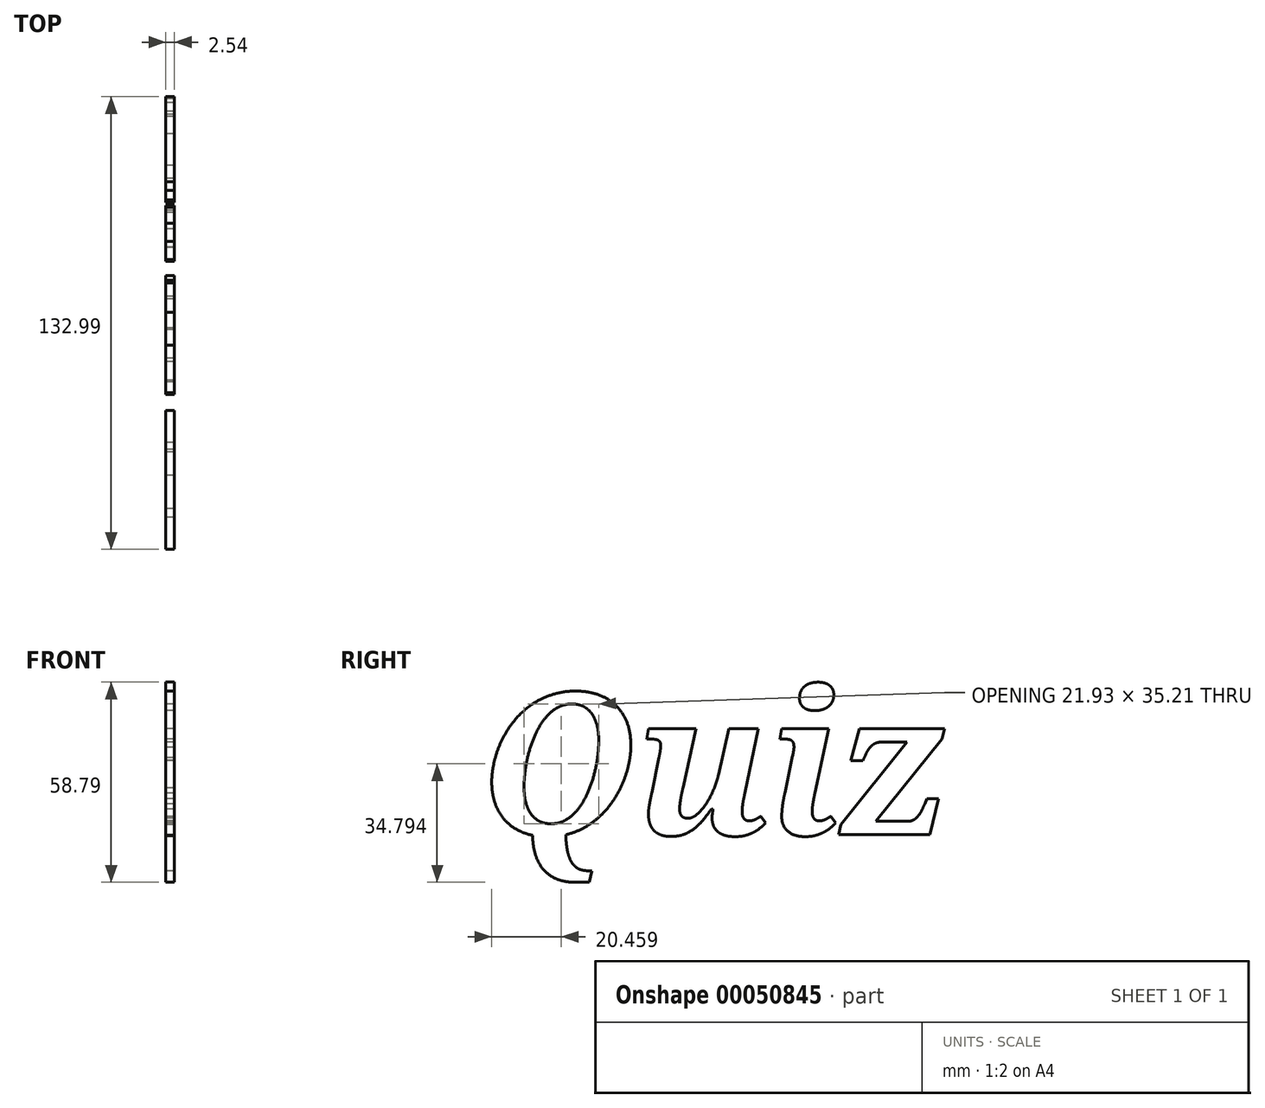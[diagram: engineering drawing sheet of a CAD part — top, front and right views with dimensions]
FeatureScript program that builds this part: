
annotation { "Feature Type Name" : "Feature", "Feature Type Description" : "" }
export const myFeature = defineFeature(function(context is Context, id is Id, definition is map)
    precondition{}
    {
        {
            var Q0;
            Q0=qCreatedBy(makeId("Right.planeOp"),FACE);
            var sketch = newSketch(context, id + "F0", { "sketchPlane" : qUnion([Q0])});
            skText(sketch, "E0", { "text": "Quiz", "fontName": "NotoSerif-BoldItalic.ttf"});
            const initialGuessF0  = {"E0": [-0.06831, -0.01958, 1, 0, 0.0419]};
            skSetInitialGuess(sketch, initialGuessF0);
            skSolve(sketch);
        }
        {
            var Q0;
            Q0 = qSketchRegion(id + "F0", true);
            extrude(context, id + "F1", {"entities" : qUnion([Q0]), "depth" : 2.54 * mm});
        }
    });
